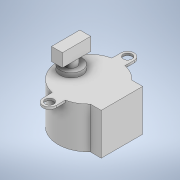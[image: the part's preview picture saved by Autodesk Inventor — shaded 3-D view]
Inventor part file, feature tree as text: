
AUTODESK INVENTOR PART (.ipt)
format: ipt  version: 2022 (Build 260153000, 153)  size: 173,568 bytes
history: native  units: mm
features: extrude x6, sketch x6, projected_geometry x2
ambient origin geometry x8: Origin, YZ Plane, XZ Plane, XY Plane, X Axis, Y Axis, Z Axis, Center Point
bodies: Solid1 (feature_tree)
feature tree (14):
  extrude  "Extrusion1"  Depth=19.0mm TaperAngle=0.0deg
  extrude  "Extrusion2"  Depth=19.0mm
  extrude  "Extrusion3"  Depth=3.9mm
  extrude  "Extrusion4"  Depth=1.0mm TaperAngle=0.0deg
  extrude  "Extrusion5"  Depth=6.0mm
  extrude  "Extrusion6"  Depth=5.0mm
  sketch  "Sketch1"  dims[d0=28.0mm d1=19.0mm d2=0.0mm]
  sketch  "Sketch2"  dims[d3=5.0mm d4=19.0mm]
  sketch  "Sketch3"  dims[d5=4.0mm d6=3.9mm]
  sketch  "Sketch4"  dims[d7=3.0mm d8=1.0mm d9=0.0mm]
  sketch  "Sketch5"  dims[d10=10.0mm d11=6.0mm]
  projected_geometry  "Projected Loop1"
  sketch  "Sketch6"  dims[d12=2.0mm d13=0.0mm d14=5.0mm d15=9.0mm d16=0.0mm d19=3.0mm d20=6.0mm d21=0.0mm d22=5.0mm d23=13.0mm d24=10.0mm d25=0.0mm]
  projected_geometry  "Projected Loop2"
